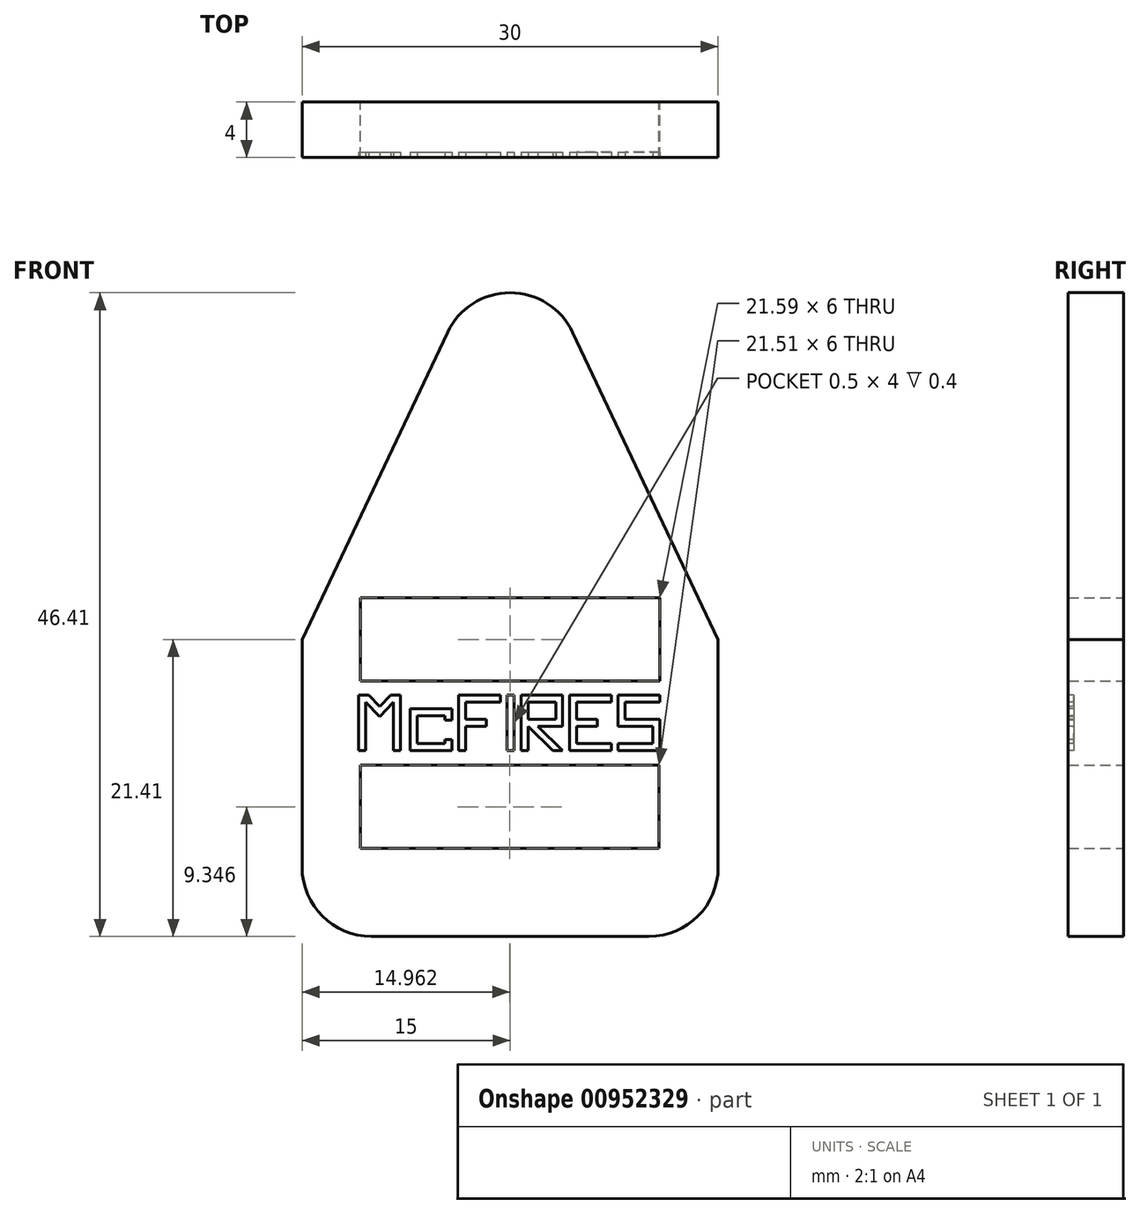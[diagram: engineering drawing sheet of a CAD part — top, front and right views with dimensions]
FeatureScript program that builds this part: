
annotation { "Feature Type Name" : "Feature", "Feature Type Description" : "" }
export const myFeature = defineFeature(function(context is Context, id is Id, definition is map)
    precondition{}
    {
        {
            var Q0;
            Q0=qCreatedBy(makeId("Front.planeOp"),FACE);
            var sketch = newSketch(context, id + "F0", { "sketchPlane" : qUnion([Q0])});
            skLineSegment(sketch, "E0.bottom", {"start": v(-5.53, 20) * mm, "end": v(5.53, 20) * mm});
            skLineSegment(sketch, "E0.top", {"start": v(-15, 0) * mm, "end": v(15, 0) * mm});
            skLineSegment(sketch, "E1.bottom", {"start": v(-10.8, 3) * mm, "end": v(10.8, 3) * mm});
            skLineSegment(sketch, "E1.top", {"start": v(-10.8, -3) * mm, "end": v(10.8, -3) * mm});
            skLineSegment(sketch, "E1.left", {"start": v(-10.8, 3) * mm, "end": v(-10.8, -3) * mm});
            skLineSegment(sketch, "E1.right", {"start": v(10.8, 3) * mm, "end": v(10.8, -3) * mm});
            skPoint(sketch, "E1.middle", {"position": v(0, 0) * mm});
            skCircle(sketch, "E2", {"center": v(0, 20) * mm, "radius": 5 * mm});
            skLineSegment(sketch, "E3", {"start": v(-4.52, 22.14) * mm, "end": v(-15, 0) * mm});
            skLineSegment(sketch, "E4", {"start": v(4.52, 22.14) * mm, "end": v(15, 0) * mm});
            skPoint(sketch, "E0.left.start.orphan", {"position": v(-15, 20) * mm});
            skLineSegment(sketch, "E5.bottom", {"start": v(-15, 0) * mm, "end": v(15, 0) * mm, "construction": true});
            skLineSegment(sketch, "E5.top", {"start": v(-10, -21.4) * mm, "end": v(10, -21.4) * mm});
            skLineSegment(sketch, "E5.left", {"start": v(-15, 0) * mm, "end": v(-15, -16.4) * mm});
            skLineSegment(sketch, "E5.right", {"start": v(15, 0) * mm, "end": v(15, -16.4) * mm});
            skPoint(sketch, "E6.visualSharp", {"position": v(-15, -21.4) * mm});
            skArc(sketch, "E6.filletArc", {"start": v(-15, -16.4) * mm, "mid": v(-13.54, -19.94) * mm, "end": v(-10, -21.4) * mm});
            skPoint(sketch, "E7.visualSharp", {"position": v(15, -21.4) * mm});
            skArc(sketch, "E7.filletArc", {"start": v(10, -21.4) * mm, "mid": v(13.54, -19.94) * mm, "end": v(15, -16.4) * mm});
            skLineSegment(sketch, "E8.bottom", {"start": v(-10.8, -9.06) * mm, "end": v(10.72, -9.06) * mm});
            skLineSegment(sketch, "E8.top", {"start": v(-10.8, -15.06) * mm, "end": v(10.72, -15.06) * mm});
            skLineSegment(sketch, "E8.left", {"start": v(-10.8, -9.06) * mm, "end": v(-10.8, -15.06) * mm});
            skLineSegment(sketch, "E8.right", {"start": v(10.72, -9.06) * mm, "end": v(10.72, -15.06) * mm});
            skLineSegment(sketch, "E9", {"start": v(-10.8, -3) * mm, "end": v(-10.8, -9.06) * mm});
            skSolve(sketch);
        }
        {
            var Q0;
            {var subQ3=sQuery(id+"F0.wireOp",EDGE,"E4");var subQ5=sQuery(id+"F0.wireOp",EDGE,"ONNQYCR8-6WIt-iKHQ-mnM0-f44IPgjX30Gc");var subQ8=makeQuery(id+"F0.imprint","INTERSECT",VERTEX,{"derivedFrom":[subQ5,subQ3]});Q0=makeQuery(id+"F0.imprint","IMPRINT",FACE,{"disambiguationData":[TD([[makeQuery(id+"F0.imprint","IMPRINT",EDGE,{"disambiguationData":[TD([[subQ8,-1.0]])],"derivedFrom":subQ5}),1.0]])]});}
            var Q1;
            {var subQ0=sQuery(id+"F0.wireOp",EDGE,"E2");var subQ1=sQuery(id+"F0.wireOp",EDGE,"ONNQYCR8-6WIt-iKHQ-mnM0-f44IPgjX30Gc");var subQ2=makeQuery(id+"F0.imprint","INTERSECT",VERTEX,{"derivedFrom":[subQ1,subQ0]});Q1=makeQuery(id+"F0.imprint","IMPRINT",FACE,{"disambiguationData":[TD([[makeQuery(id+"F0.imprint","IMPRINT",EDGE,{"disambiguationData":[TD([[subQ2,-1.0]])],"derivedFrom":subQ1}),-1.0]])]});}
            var Q2;
            {var subQ0=sQuery(id+"F0.wireOp",EDGE,"E4");var subQ1=sQuery(id+"F0.wireOp",EDGE,"ONNQYCR8-6WIt-iKHQ-mnM0-f44IPgjX30Gc");var subQ2=makeQuery(id+"F0.imprint","INTERSECT",VERTEX,{"derivedFrom":[subQ1,subQ0]});Q2=makeQuery(id+"F0.imprint","IMPRINT",FACE,{"disambiguationData":[TD([[makeQuery(id+"F0.imprint","IMPRINT",EDGE,{"disambiguationData":[TD([[subQ2,-1.0]])],"derivedFrom":subQ1}),-1.0]])]});}
            var Q3;
            {var subQ0=sQuery(id+"F0.wireOp",EDGE,"E2");var subQ1=sQuery(id+"F0.wireOp",EDGE,"E0.bottom");var subQ2=makeQuery(id+"F0.imprint","INTERSECT",VERTEX,{"disambiguationData":[OD(0.0)],"derivedFrom":[subQ1,subQ0]});Q3=makeQuery(id+"F0.imprint","IMPRINT",FACE,{"disambiguationData":[TD([[makeQuery(id+"F0.imprint","IMPRINT",EDGE,{"disambiguationData":[TD([[subQ2,-1.0]])],"derivedFrom":subQ1}),-1.0]])]});}
            var Q4;
            {var subQ0=sQuery(id+"F0.wireOp",EDGE,"E2");var subQ1=sQuery(id+"F0.wireOp",EDGE,"E0.bottom");var subQ2=makeQuery(id+"F0.imprint","INTERSECT",VERTEX,{"disambiguationData":[OD(0.0)],"derivedFrom":[subQ1,subQ0]});Q4=makeQuery(id+"F0.imprint","IMPRINT",FACE,{"disambiguationData":[TD([[makeQuery(id+"F0.imprint","IMPRINT",EDGE,{"disambiguationData":[TD([[subQ2,-1.0]])],"derivedFrom":subQ1}),1.0]])]});}
            var Q5;
            {var subQ0=sQuery(id+"F0.wireOp",EDGE,"E1.bottom");Q5=makeQuery(id+"F0.imprint","IMPRINT",FACE,{"disambiguationData":[TD([[makeQuery(id+"F0.imprint","IMPRINT",EDGE,{"derivedFrom":subQ0}),1.0]])]});}
            var Q6;
            {var subQ9=sQuery(id+"F0.wireOp",EDGE,"E1.top");Q6=makeQuery(id+"F0.imprint","IMPRINT",FACE,{"disambiguationData":[TD([[makeQuery(id+"F0.imprint","IMPRINT",EDGE,{"derivedFrom":subQ9}),-1.0]])]});}
            var Q7;
            {var subQ0=sQuery(id+"F0.wireOp",EDGE,"E3");var subQ1=sQuery(id+"F0.wireOp",EDGE,"E0.bottom");var subQ2=makeQuery(id+"F0.imprint","INTERSECT",VERTEX,{"derivedFrom":[subQ1,subQ0]});Q7=makeQuery(id+"F0.imprint","IMPRINT",FACE,{"disambiguationData":[TD([[makeQuery(id+"F0.imprint","IMPRINT",EDGE,{"disambiguationData":[TD([[subQ2,-1.0]])],"derivedFrom":subQ1}),1.0]])]});}
            var Q8;
            {var subQ0=sQuery(id+"F0.wireOp",EDGE,"E2");var subQ1=sQuery(id+"F0.wireOp",EDGE,"E0.bottom");var subQ2=makeQuery(id+"F0.imprint","INTERSECT",VERTEX,{"disambiguationData":[OD(1.0)],"derivedFrom":[subQ1,subQ0]});Q8=makeQuery(id+"F0.imprint","IMPRINT",FACE,{"disambiguationData":[TD([[makeQuery(id+"F0.imprint","IMPRINT",EDGE,{"disambiguationData":[TD([[subQ2,-1.0]])],"derivedFrom":subQ1}),1.0]])]});}
            extrude(context, id + "F1", {"entities" : qUnion([Q0, Q1, Q2, Q3, Q4, Q5, Q6, Q7, Q8]), "depth" : 4 * mm, "offsetDistance" : 25 * mm});
        }
        {
            var Q0;
            Q0=makeQuery(id+"F1.opExtrude","CAP_FACE",FACE,{"disambiguationData":[OSD([sQuery(id+"F0.wireOp",EDGE,"ONNQYCR8-6WIt-iKHQ-mnM0-f44IPgjX30Gc"),sQuery(id+"F0.wireOp",EDGE,"E1.bottom"),sQuery(id+"F0.wireOp",EDGE,"E1.top"),sQuery(id+"F0.wireOp",EDGE,"E1.left"),sQuery(id+"F0.wireOp",EDGE,"E1.right"),sQuery(id+"F0.wireOp",EDGE,"2yZK4rqS-Fx8S-sqmz-Zjop-CJASyxLAb1NZ"),sQuery(id+"F0.wireOp",EDGE,"E2"),sQuery(id+"F0.wireOp",EDGE,"E3"),sQuery(id+"F0.wireOp",EDGE,"E4")])],"isStart":false});
            var sketch = newSketch(context, id + "F2", { "sketchPlane" : qUnion([Q0])});
            skLineSegment(sketch, "E10.bottom", {"start": v(-10.9, -4) * mm, "end": v(-10.4, -4) * mm});
            skLineSegment(sketch, "E10.top", {"start": v(-10.9, -8) * mm, "end": v(-10.4, -8) * mm});
            skLineSegment(sketch, "E10.left", {"start": v(-10.9, -4) * mm, "end": v(-10.9, -8) * mm});
            skLineSegment(sketch, "E10.right", {"start": v(-10.4, -4.5) * mm, "end": v(-10.4, -8) * mm});
            skLineSegment(sketch, "E11.bottom", {"start": v(-8.4, -4) * mm, "end": v(-7.9, -4) * mm});
            skLineSegment(sketch, "E11.top", {"start": v(-8.4, -8) * mm, "end": v(-7.9, -8) * mm});
            skLineSegment(sketch, "E11.left", {"start": v(-8.4, -4.5) * mm, "end": v(-8.4, -8) * mm});
            skLineSegment(sketch, "E11.right", {"start": v(-7.9, -4) * mm, "end": v(-7.9, -8) * mm});
            skLineSegment(sketch, "E12.bottom", {"start": v(-7.2, -5) * mm, "end": v(-4.2, -5) * mm});
            skLineSegment(sketch, "E12.top", {"start": v(-7.2, -8) * mm, "end": v(-4.2, -8) * mm});
            skLineSegment(sketch, "E12.left", {"start": v(-7.2, -5) * mm, "end": v(-7.2, -8) * mm});
            skLineSegment(sketch, "E12.right", {"start": v(-4.2, -5) * mm, "end": v(-4.2, -8) * mm});
            skLineSegment(sketch, "E13.bottom", {"start": v(-3.7, -4) * mm, "end": v(-0.7, -4) * mm});
            skLineSegment(sketch, "E13.top", {"start": v(-3.7, -8) * mm, "end": v(-3.2, -8) * mm});
            skLineSegment(sketch, "E13.left", {"start": v(-3.7, -4) * mm, "end": v(-3.7, -8) * mm});
            skLineSegment(sketch, "E14.bottom", {"start": v(-0.2, -4) * mm, "end": v(0.3, -4) * mm});
            skLineSegment(sketch, "E14.top", {"start": v(-0.2, -8) * mm, "end": v(0.3, -8) * mm});
            skLineSegment(sketch, "E14.left", {"start": v(-0.2, -4) * mm, "end": v(-0.2, -8) * mm});
            skLineSegment(sketch, "E14.right", {"start": v(0.3, -4) * mm, "end": v(0.3, -8) * mm});
            skLineSegment(sketch, "E15.bottom", {"start": v(0.8, -4) * mm, "end": v(3.8, -4) * mm});
            skLineSegment(sketch, "E15.top", {"start": v(0.8, -8) * mm, "end": v(3.8, -8) * mm});
            skLineSegment(sketch, "E15.left", {"start": v(0.8, -4) * mm, "end": v(0.8, -8) * mm});
            skLineSegment(sketch, "E15.right", {"start": v(3.8, -4) * mm, "end": v(3.8, -8) * mm});
            skLineSegment(sketch, "E16.bottom", {"start": v(4.3, -4) * mm, "end": v(7.3, -4) * mm});
            skLineSegment(sketch, "E16.top", {"start": v(4.3, -8) * mm, "end": v(7.3, -8) * mm});
            skLineSegment(sketch, "E16.left", {"start": v(4.3, -4) * mm, "end": v(4.3, -8) * mm});
            skLineSegment(sketch, "E16.right", {"start": v(7.3, -4) * mm, "end": v(7.3, -4.5) * mm});
            skLineSegment(sketch, "E17.bottom", {"start": v(7.8, -4) * mm, "end": v(10.8, -4) * mm});
            skLineSegment(sketch, "E17.top", {"start": v(7.8, -8) * mm, "end": v(10.8, -8) * mm});
            skLineSegment(sketch, "E17.left", {"start": v(7.8, -4) * mm, "end": v(7.8, -8) * mm});
            skLineSegment(sketch, "E17.right", {"start": v(10.8, -4) * mm, "end": v(10.8, -8) * mm});
            skLineSegment(sketch, "E18", {"start": v(-10.4, -4) * mm, "end": v(-10.2, -4) * mm});
            skLineSegment(sketch, "E19", {"start": v(-10.2, -4) * mm, "end": v(-9.4, -4.85) * mm});
            skLineSegment(sketch, "E20", {"start": v(-9.4, -4.85) * mm, "end": v(-8.6, -4) * mm});
            skLineSegment(sketch, "E21", {"start": v(-8.6, -4) * mm, "end": v(-8.4, -4) * mm});
            skLineSegment(sketch, "E22", {"start": v(-10.4, -4.5) * mm, "end": v(-10.4, -4.5) * mm});
            skLineSegment(sketch, "E23", {"start": v(-10.4, -4.5) * mm, "end": v(-9.4, -5.55) * mm});
            skLineSegment(sketch, "E24", {"start": v(-9.4, -5.55) * mm, "end": v(-8.42, -4.5) * mm});
            skLineSegment(sketch, "E25", {"start": v(-8.42, -4.5) * mm, "end": v(-8.4, -4.5) * mm});
            skLineSegment(sketch, "E26.bottom", {"start": v(-6.7, -5.5) * mm, "end": v(-4.7, -5.5) * mm});
            skLineSegment(sketch, "E26.top", {"start": v(-6.7, -7.5) * mm, "end": v(-4.7, -7.5) * mm});
            skLineSegment(sketch, "E26.left", {"start": v(-6.7, -5.5) * mm, "end": v(-6.7, -7.5) * mm});
            skLineSegment(sketch, "E26.right", {"start": v(-4.7, -5.5) * mm, "end": v(-4.7, -5.8) * mm});
            skLineSegment(sketch, "E27.bottom", {"start": v(-4.7, -5.8) * mm, "end": v(-4.2, -5.8) * mm});
            skLineSegment(sketch, "E27.top", {"start": v(-4.7, -7.2) * mm, "end": v(-4.2, -7.2) * mm});
            skLineSegment(sketch, "E28.bottom", {"start": v(-3.2, -4.5) * mm, "end": v(-0.7, -4.5) * mm});
            skLineSegment(sketch, "E28.top", {"start": v(-3.2, -5.75) * mm, "end": v(-1.7, -5.75) * mm});
            skLineSegment(sketch, "E28.left", {"start": v(-3.2, -4.5) * mm, "end": v(-3.2, -5.75) * mm});
            skLineSegment(sketch, "E29.bottom", {"start": v(-3.2, -6.25) * mm, "end": v(-1.7, -6.25) * mm});
            skLineSegment(sketch, "E29.left", {"start": v(-3.2, -6.25) * mm, "end": v(-3.2, -8) * mm});
            skLineSegment(sketch, "E30.left", {"start": v(-1.7, -5.75) * mm, "end": v(-1.7, -6.25) * mm});
            skPoint(sketch, "E31.oppositeSnap0", {"position": v(-0.1, -5.75) * mm});
            skLineSegment(sketch, "E31.bottom", {"start": v(1.3, -4.5) * mm, "end": v(3.3, -4.5) * mm});
            skLineSegment(sketch, "E31.top", {"start": v(1.3, -5.75) * mm, "end": v(3.3, -5.75) * mm});
            skLineSegment(sketch, "E31.left", {"start": v(1.3, -4.5) * mm, "end": v(1.3, -5.75) * mm});
            skLineSegment(sketch, "E31.right", {"start": v(3.3, -4.5) * mm, "end": v(3.3, -5.75) * mm});
            skLineSegment(sketch, "E32", {"start": v(1.3, -6.25) * mm, "end": v(1.3, -8) * mm});
            skLineSegment(sketch, "E33", {"start": v(2, -6.25) * mm, "end": v(3.8, -6.25) * mm});
            skLineSegment(sketch, "E34", {"start": v(2, -6.25) * mm, "end": v(3.8, -8) * mm});
            skLineSegment(sketch, "E35.bottom", {"start": v(7.3, -4.5) * mm, "end": v(4.8, -4.5) * mm});
            skLineSegment(sketch, "E35.right", {"start": v(4.8, -4.5) * mm, "end": v(4.8, -5.75) * mm});
            skLineSegment(sketch, "E36.top", {"start": v(4.8, -7.5) * mm, "end": v(7.3, -7.5) * mm});
            skLineSegment(sketch, "E36.left", {"start": v(4.8, -6.25) * mm, "end": v(4.8, -7.5) * mm});
            skLineSegment(sketch, "E37.bottom", {"start": v(10.8, -4.5) * mm, "end": v(8.3, -4.5) * mm});
            skLineSegment(sketch, "E37.top", {"start": v(10.8, -5.75) * mm, "end": v(8.3, -5.75) * mm});
            skLineSegment(sketch, "E37.left", {"start": v(10.8, -4.5) * mm, "end": v(10.8, -5.75) * mm});
            skLineSegment(sketch, "E37.right", {"start": v(8.3, -4.5) * mm, "end": v(8.3, -5.75) * mm});
            skLineSegment(sketch, "E38.bottom", {"start": v(7.8, -6.25) * mm, "end": v(10.3, -6.25) * mm});
            skLineSegment(sketch, "E38.top", {"start": v(7.8, -7.5) * mm, "end": v(10.3, -7.5) * mm});
            skLineSegment(sketch, "E38.left", {"start": v(7.8, -7.5) * mm, "end": v(7.8, -6.25) * mm});
            skLineSegment(sketch, "E38.right", {"start": v(10.3, -7.5) * mm, "end": v(10.3, -6.25) * mm});
            skLineSegment(sketch, "E39", {"start": v(-6.7, -7.5) * mm, "end": v(-7.2, -7.5) * mm, "construction": true});
            skLineSegment(sketch, "E40", {"start": v(-3.2, -4.5) * mm, "end": v(-3.7, -4.5) * mm, "construction": true});
            skLineSegment(sketch, "E41", {"start": v(-3.2, -4.5) * mm, "end": v(-3.2, -4) * mm, "construction": true});
            skLineSegment(sketch, "E42", {"start": v(-10.9, -8) * mm, "end": v(-7.9, -8) * mm, "construction": true});
            skLineSegment(sketch, "E43", {"start": v(-9.4, -5.55) * mm, "end": v(-9.4, -4.85) * mm, "construction": true});
            skLineSegment(sketch, "E44", {"start": v(-6.7, -7.5) * mm, "end": v(-6.7, -8) * mm, "construction": true});
            skLineSegment(sketch, "E45", {"start": v(-6.7, -5.5) * mm, "end": v(-6.7, -5) * mm, "construction": true});
            skLineSegment(sketch, "E46.trimOffspring", {"start": v(-4.7, -7.2) * mm, "end": v(-4.7, -7.5) * mm});
            skLineSegment(sketch, "E47", {"start": v(-10.4, -4) * mm, "end": v(-10.4, -4.5) * mm, "construction": true});
            skLineSegment(sketch, "E48", {"start": v(-8.4, -4) * mm, "end": v(-8.4, -4.5) * mm, "construction": true});
            skLineSegment(sketch, "E49", {"start": v(-3.2, -6.25) * mm, "end": v(-3.7, -6.25) * mm, "construction": true});
            skLineSegment(sketch, "E50", {"start": v(-0.7, -4.5) * mm, "end": v(-0.7, -4) * mm});
            skLineSegment(sketch, "E51", {"start": v(1.3, -5.75) * mm, "end": v(1.47, -5.29) * mm, "construction": true});
            skLineSegment(sketch, "E52", {"start": v(1.3, -4.5) * mm, "end": v(1.3, -4) * mm, "construction": true});
            skLineSegment(sketch, "E53", {"start": v(1.3, -6.25) * mm, "end": v(1.3, -5.75) * mm});
            skLineSegment(sketch, "E54", {"start": v(3.3, -5.75) * mm, "end": v(3.3, -6.25) * mm, "construction": true});
            skLineSegment(sketch, "E55", {"start": v(1.3, -6.25) * mm, "end": v(3.08, -8) * mm});
            skLineSegment(sketch, "E56", {"start": v(3.3, -4.5) * mm, "end": v(3.8, -4.5) * mm, "construction": true});
            skLineSegment(sketch, "E57", {"start": v(4.8, -7.5) * mm, "end": v(4.3, -7.5) * mm, "construction": true});
            skLineSegment(sketch, "E58", {"start": v(3.8, -4) * mm, "end": v(4.3, -4) * mm, "construction": true});
            skLineSegment(sketch, "E59", {"start": v(0.3, -4) * mm, "end": v(0.8, -4) * mm, "construction": true});
            skLineSegment(sketch, "E60", {"start": v(4.8, -4.5) * mm, "end": v(4.8, -4) * mm, "construction": true});
            skLineSegment(sketch, "E61.bottom", {"start": v(4.8, -5.75) * mm, "end": v(6.3, -5.75) * mm});
            skLineSegment(sketch, "E61.top", {"start": v(4.8, -6.25) * mm, "end": v(6.3, -6.25) * mm});
            skLineSegment(sketch, "E61.left", {"start": v(4.8, -5.75) * mm, "end": v(4.8, -6.25) * mm, "construction": true});
            skLineSegment(sketch, "E61.right", {"start": v(6.3, -5.75) * mm, "end": v(6.3, -6.25) * mm});
            skLineSegment(sketch, "E62", {"start": v(-3.2, -5.75) * mm, "end": v(-3.2, -6.25) * mm, "construction": true});
            skLineSegment(sketch, "E63.trimOffspring", {"start": v(7.3, -7.5) * mm, "end": v(7.3, -8) * mm});
            skLineSegment(sketch, "E64", {"start": v(8.3, -4.5) * mm, "end": v(8.3, -4) * mm, "construction": true});
            skLineSegment(sketch, "E65", {"start": v(10.3, -6.25) * mm, "end": v(10.3, -5.75) * mm, "construction": true});
            skLineSegment(sketch, "E66", {"start": v(10.3, -7.5) * mm, "end": v(10.3, -8) * mm, "construction": true});
            skLineSegment(sketch, "E67", {"start": v(8.3, -5.75) * mm, "end": v(7.8, -5.75) * mm, "construction": true});
            skLineSegment(sketch, "E68", {"start": v(10.3, -7.5) * mm, "end": v(10.8, -7.5) * mm, "construction": true});
            skLineSegment(sketch, "E69", {"start": v(7.8, -4) * mm, "end": v(7.3, -4) * mm, "construction": true});
            skSolve(sketch);
        }
        {
            var Q0;
            Q0=makeQuery(id+"F2.imprint","IMPRINT",FACE,{"disambiguationData":[TD([[makeQuery(id+"F2.imprint","IMPRINT",EDGE,{"derivedFrom":sQuery(id+"F2.wireOp",EDGE,"E10.bottom")}),-1.0]])]});
            var Q1;
            {var subQ4=sQuery(id+"F2.wireOp",EDGE,"E12.bottom");Q1=makeQuery(id+"F2.imprint","IMPRINT",FACE,{"disambiguationData":[TD([[makeQuery(id+"F2.imprint","IMPRINT",EDGE,{"derivedFrom":subQ4}),-1.0]])]});}
            var Q2;
            Q2=makeQuery(id+"F2.imprint","IMPRINT",FACE,{"disambiguationData":[TD([[makeQuery(id+"F2.imprint","IMPRINT",EDGE,{"derivedFrom":sQuery(id+"F2.wireOp",EDGE,"E13.bottom")}),-1.0]])]});
            var Q3;
            Q3=makeQuery(id+"F2.imprint","IMPRINT",FACE,{"disambiguationData":[TD([[makeQuery(id+"F2.imprint","IMPRINT",EDGE,{"derivedFrom":sQuery(id+"F2.wireOp",EDGE,"E14.bottom")}),-1.0]])]});
            var Q4;
            {var subQ2=sQuery(id+"F2.wireOp",EDGE,"E15.bottom");Q4=makeQuery(id+"F2.imprint","IMPRINT",FACE,{"disambiguationData":[TD([[makeQuery(id+"F2.imprint","IMPRINT",EDGE,{"derivedFrom":subQ2}),-1.0]])]});}
            var Q5;
            Q5=makeQuery(id+"F2.imprint","IMPRINT",FACE,{"disambiguationData":[TD([[makeQuery(id+"F2.imprint","IMPRINT",EDGE,{"derivedFrom":sQuery(id+"F2.wireOp",EDGE,"E16.bottom")}),-1.0]])]});
            var Q6;
            {var subQ1=sQuery(id+"F2.wireOp",EDGE,"E17.bottom");Q6=makeQuery(id+"F2.imprint","IMPRINT",FACE,{"disambiguationData":[TD([[makeQuery(id+"F2.imprint","IMPRINT",EDGE,{"derivedFrom":subQ1}),-1.0]])]});}
            extrude(context, id + "F3", {"entities" : qUnion([Q0, Q1, Q2, Q3, Q4, Q5, Q6]), "operationType" : NewBodyOperationType.REMOVE, "oppositeDirection" : true, "depth" : 0.4 * mm, "offsetDistance" : 25 * mm});
        }
    });
